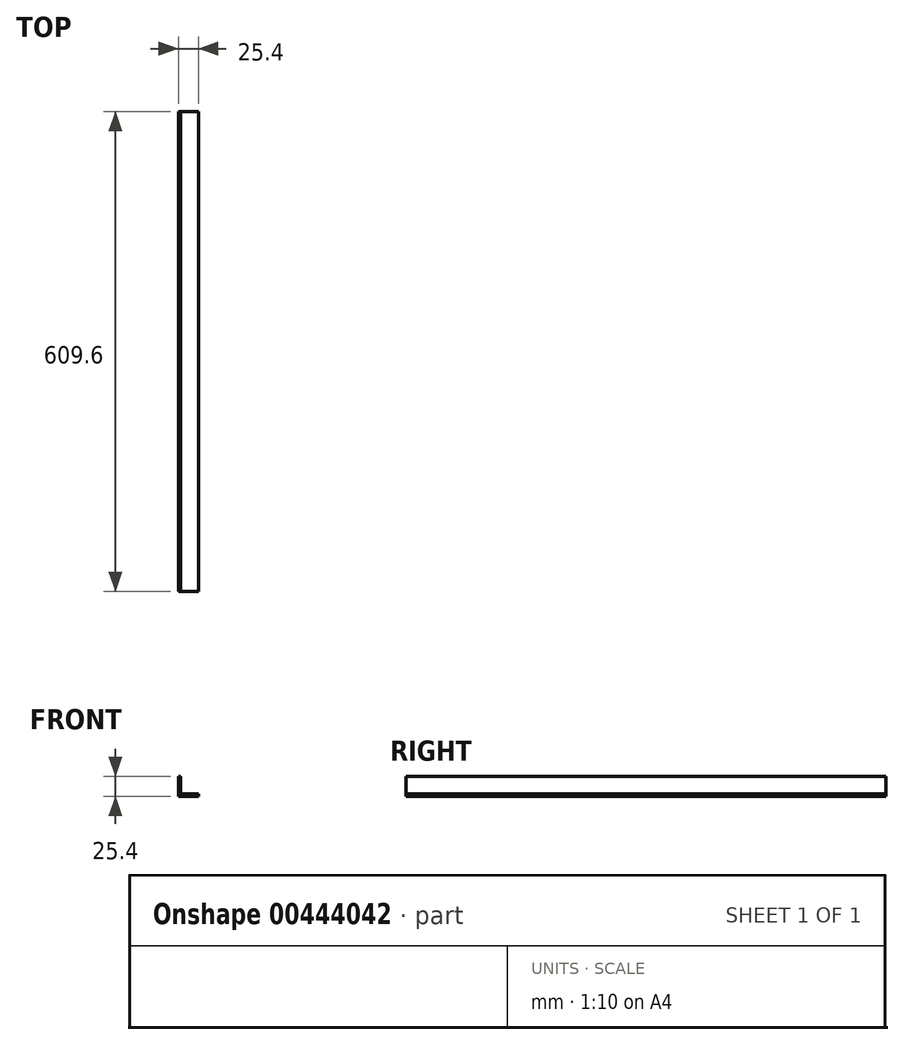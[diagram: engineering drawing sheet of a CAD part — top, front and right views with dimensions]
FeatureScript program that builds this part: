
annotation { "Feature Type Name" : "Feature", "Feature Type Description" : "" }
export const myFeature = defineFeature(function(context is Context, id is Id, definition is map)
    precondition{}
    {
        {
            var Q0;
            Q0=qCreatedBy(makeId("Front.planeOp"),FACE);
            var sketch = newSketch(context, id + "F0", { "sketchPlane" : qUnion([Q0])});
            skLineSegment(sketch, "E0", {"start": v(0, 0) * mm, "end": v(0, 25.4) * mm});
            skLineSegment(sketch, "E1", {"start": v(0, 25.4) * mm, "end": v(3.17, 25.4) * mm});
            skLineSegment(sketch, "E2", {"start": v(3.17, 25.4) * mm, "end": v(3.18, 3.17) * mm});
            skLineSegment(sketch, "E3", {"start": v(3.18, 3.17) * mm, "end": v(25.4, 3.18) * mm});
            skLineSegment(sketch, "E4", {"start": v(25.4, 3.18) * mm, "end": v(25.4, 0) * mm});
            skLineSegment(sketch, "E5", {"start": v(25.4, 0) * mm, "end": v(0, 0) * mm});
            skSolve(sketch);
        }
        {
            var Q0;
            Q0=qSketchRegion(id+"F0",true);
            extrude(context, id + "F1", {"entities" : qUnion([Q0]), "depth" : 609.6 * mm});
        }
    });
